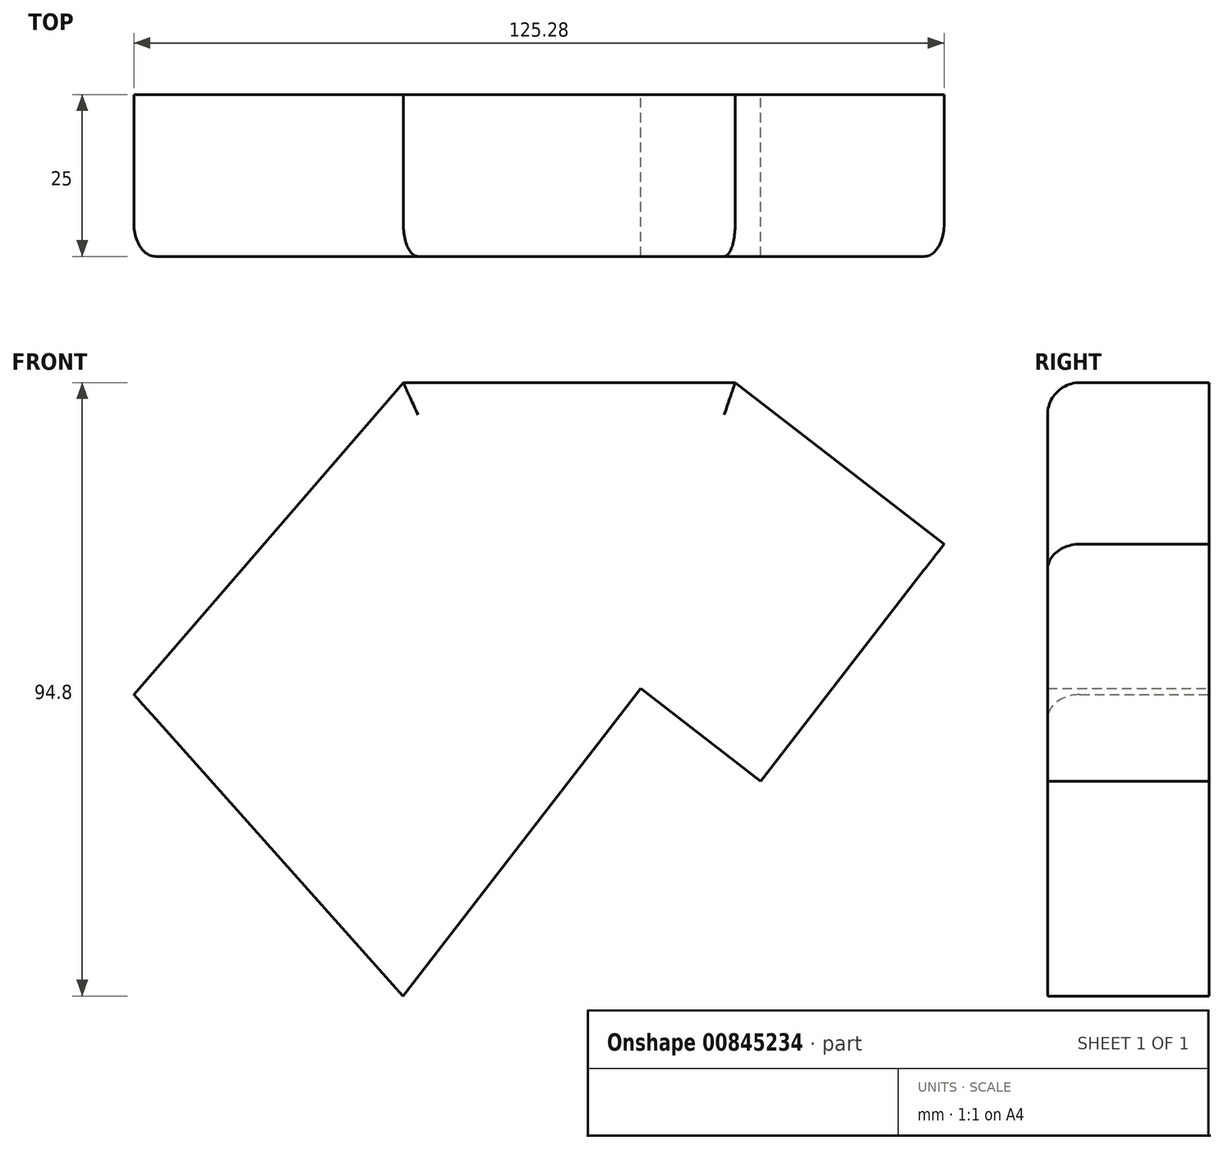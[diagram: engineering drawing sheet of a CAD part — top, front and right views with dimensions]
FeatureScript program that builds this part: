
annotation { "Feature Type Name" : "Feature", "Feature Type Description" : "" }
export const myFeature = defineFeature(function(context is Context, id is Id, definition is map)
    precondition{}
    {
        {
            var Q0;
            Q0=qCreatedBy(makeId("Front.planeOp"),FACE);
            var sketch = newSketch(context, id + "F0", { "sketchPlane" : qUnion([Q0])});
            skLineSegment(sketch, "E0", {"start": v(-16.46, -33.18) * mm, "end": v(20.29, 14.35) * mm});
            skLineSegment(sketch, "E1", {"start": v(20.29, 14.35) * mm, "end": v(38.85, 0) * mm});
            skLineSegment(sketch, "E2", {"start": v(38.85, 0) * mm, "end": v(67.18, 36.65) * mm});
            skLineSegment(sketch, "E3", {"start": v(67.18, 36.65) * mm, "end": v(34.88, 61.62) * mm});
            skLineSegment(sketch, "E4", {"start": v(34.88, 61.62) * mm, "end": v(-16.44, 61.62) * mm});
            skLineSegment(sketch, "E5", {"start": v(-16.44, 61.62) * mm, "end": v(-58.1, 13.41) * mm});
            skLineSegment(sketch, "E6", {"start": v(-58.1, 13.41) * mm, "end": v(-16.46, -33.18) * mm});
            skSolve(sketch);
        }
        {
            var Q0;
            Q0=makeQuery(id+"F0.imprint","IMPRINT",FACE,{"disambiguationData":[TD([[makeQuery(id+"F0.imprint","IMPRINT",EDGE,{"derivedFrom":sQuery(id+"F0.wireOp",EDGE,"E0")}),1.0]])]});
            extrude(context, id + "F1", {"entities" : qUnion([Q0]), "depth" : 25 * mm, "offsetDistance" : 25 * mm});
        }
        {
            var Q0;
            Q0=makeQuery(id+"F1.opExtrude","CAP_EDGE",EDGE,{"disambiguationData":[OSD([sQuery(id+"F0.wireOp",EDGE,"E3")])],"isStart":false});
            var Q1;
            Q1=makeQuery(id+"F1.opExtrude","CAP_EDGE",EDGE,{"disambiguationData":[OSD([sQuery(id+"F0.wireOp",EDGE,"E4")])],"isStart":false});
            var Q2;
            Q2=makeQuery(id+"F1.opExtrude","CAP_EDGE",EDGE,{"disambiguationData":[OSD([sQuery(id+"F0.wireOp",EDGE,"E5")])],"isStart":false});
            fillet(context, id + "F2", {"entities" : qUnion([Q0, Q1, Q2]), "tangentPropagation" : true, "radius" : 5 * mm, "defaultsChanged" : false, "vertexSettings" : [], "allowEdgeOverflow" : false});
        }
    });
